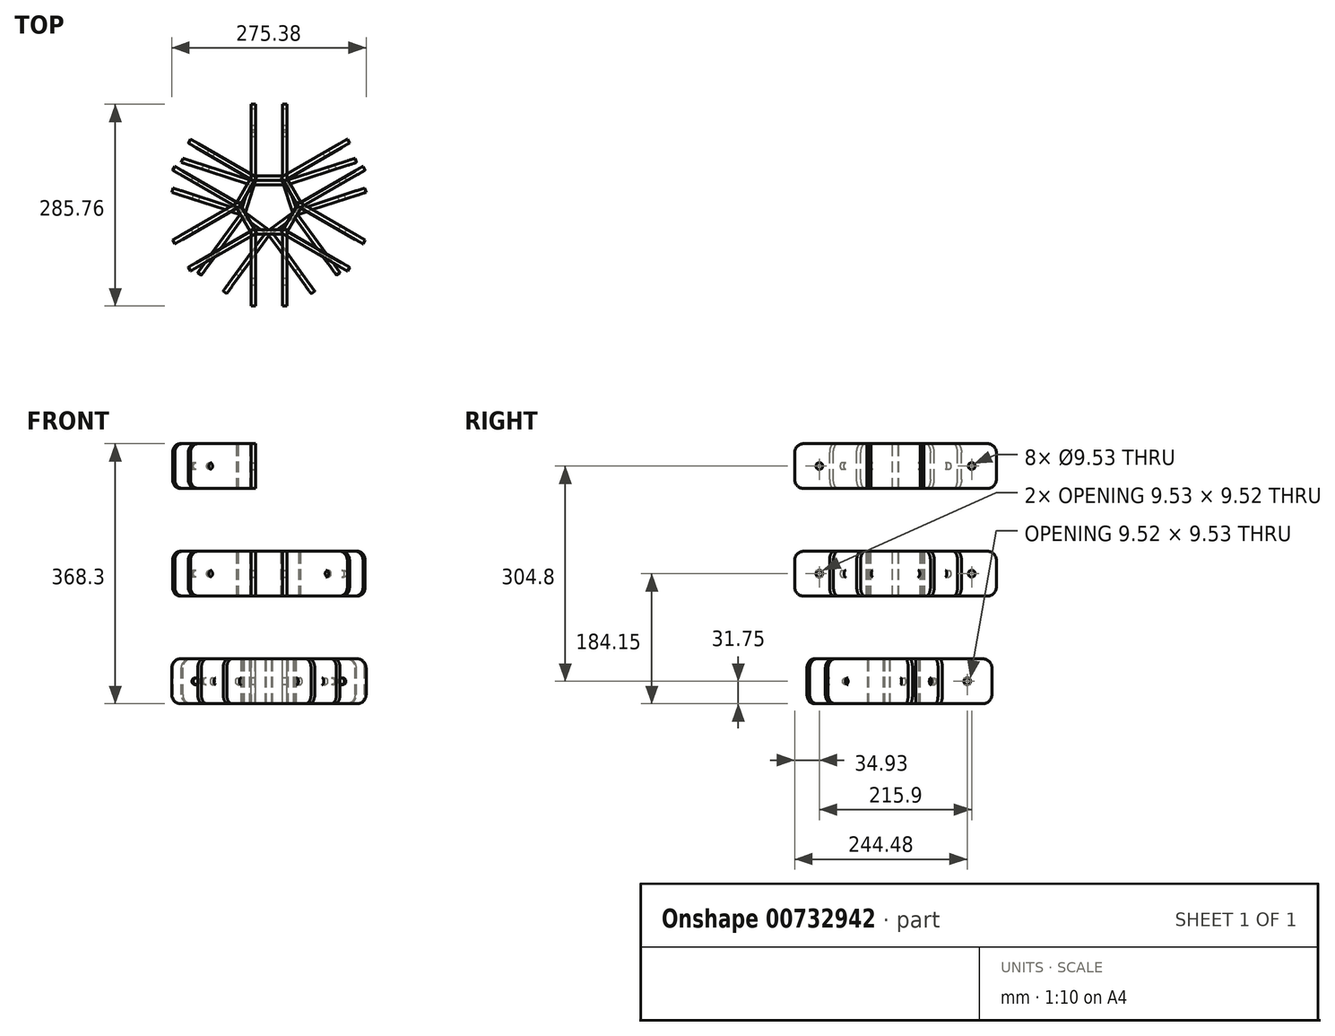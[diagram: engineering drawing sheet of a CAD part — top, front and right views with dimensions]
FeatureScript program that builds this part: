
annotation { "Feature Type Name" : "Feature", "Feature Type Description" : "" }
export const myFeature = defineFeature(function(context is Context, id is Id, definition is map)
    precondition{}
    {
        {
            var Q0;
            Q0=qCreatedBy(makeId("Top.planeOp"),FACE);
            var sketch = newSketch(context, id + "F0", { "sketchPlane" : qUnion([Q0])});
            skLineSegment(sketch, "E0.bottom", {"start": v(-25.4, 136.53) * mm, "end": v(-19.05, 136.53) * mm});
            skLineSegment(sketch, "E0.top", {"start": v(-25.4, 28.58) * mm, "end": v(25.4, 28.58) * mm});
            skLineSegment(sketch, "E0.left", {"start": v(-25.4, 136.53) * mm, "end": v(-25.4, 28.58) * mm});
            skLineSegment(sketch, "E0.right", {"start": v(25.4, 136.53) * mm, "end": v(25.4, 28.58) * mm});
            skLineSegment(sketch, "E1.bottom", {"start": v(19.05, 34.93) * mm, "end": v(-19.05, 34.93) * mm});
            skLineSegment(sketch, "E1.left", {"start": v(19.05, 34.93) * mm, "end": v(19.05, 136.53) * mm});
            skLineSegment(sketch, "E1.right", {"start": v(-19.05, 34.93) * mm, "end": v(-19.05, 136.53) * mm});
            skLineSegment(sketch, "E2.trimOffspring", {"start": v(19.05, 136.53) * mm, "end": v(25.4, 136.53) * mm});
            skSolve(sketch);
        }
        {
            var Q0;
            Q0 = qSketchRegion(id + "F0", true);
            extrude(context, id + "F1", {"entities" : qUnion([Q0]), "oppositeDirection" : true, "depth" : 63.5 * mm, "offsetDistance" : 25.4 * mm});
        }
        {
            var Q0;
            Q0=makeQuery(id+"F1.opExtrude","SWEPT_FACE",FACE,{"disambiguationData":[OSD([sQuery(id+"F0.wireOp",EDGE,"E0.left")])]});
            var sketch = newSketch(context, id + "F2", { "sketchPlane" : qUnion([Q0])});
            skCircle(sketch, "E3", {"center": v(-101.6, -31.75) * mm, "radius": 4.76 * mm});
            skSolve(sketch);
        }
        {
            var Q0;
            Q0 = qSketchRegion(id + "F2", true);
            extrude(context, id + "F3", {"entities" : qUnion([Q0]), "operationType" : NewBodyOperationType.REMOVE, "endBound" : BoundingType.THROUGH_ALL, "oppositeDirection" : true, "depth" : 25.4 * mm, "offsetDistance" : 25.4 * mm});
        }
        {
            var Q0;
            Q0=qCreatedBy(makeId("Right.planeOp"),FACE);
            var sketch = newSketch(context, id + "F4", { "sketchPlane" : qUnion([Q0])});
            skLineSegment(sketch, "E4", {"start": v(0, 0) * mm, "end": v(0, 467.4) * mm, "construction": true});
            skSolve(sketch);
        }
        {
            var Q0;
            Q0=makeQuery(id+"F1.opExtrude","CAP_EDGE",EDGE,{"disambiguationData":[OSD([sQuery(id+"F0.wireOp",EDGE,"E0.bottom")])],"isStart":false});
            var Q1;
            Q1=makeQuery(id+"F1.opExtrude","CAP_EDGE",EDGE,{"disambiguationData":[OSD([sQuery(id+"F0.wireOp",EDGE,"E2.trimOffspring")])],"isStart":false});
            var Q2;
            Q2=makeQuery(id+"F1.opExtrude","CAP_EDGE",EDGE,{"disambiguationData":[OSD([sQuery(id+"F0.wireOp",EDGE,"E2.trimOffspring")])],"isStart":true});
            var Q3;
            Q3=makeQuery(id+"F1.opExtrude","CAP_EDGE",EDGE,{"disambiguationData":[OSD([sQuery(id+"F0.wireOp",EDGE,"E0.bottom")])],"isStart":true});
            fillet(context, id + "F5", {"entities" : qUnion([Q0, Q1, Q2, Q3]), "radius" : 12.7 * mm, "tangentPropagation" : true, "allowEdgeOverflow" : false});
        }
        {
            var Q0;
            Q0=makeQuery(id+"F1.opExtrude","SWEPT_BODY",BODY,{"disambiguationData":[OSD([sQuery(id+"F0.wireOp",EDGE,"E0.bottom"),sQuery(id+"F0.wireOp",EDGE,"E0.top"),sQuery(id+"F0.wireOp",EDGE,"E0.left"),sQuery(id+"F0.wireOp",EDGE,"E0.right"),sQuery(id+"F0.wireOp",EDGE,"E1.bottom"),sQuery(id+"F0.wireOp",EDGE,"E1.left"),sQuery(id+"F0.wireOp",EDGE,"E1.right"),sQuery(id+"F0.wireOp",EDGE,"E2.trimOffspring")])]});
            transform(context, id + "F6", {"entities" : qUnion([Q0]), "transformType" : TransformType.TRANSLATION_3D, "dx" : 0 * mm, "dy" : 6.35 * mm, "dz" : 152.4 * mm, "makeCopy" : true});
        }
        {
            var Q0;
            Q0=makeQuery(id+"F6.opPattern","COPY",BODY,{"derivedFrom":makeQuery(id+"F1.opExtrude","SWEPT_BODY",BODY,{"disambiguationData":[OSD([sQuery(id+"F0.wireOp",EDGE,"E0.bottom"),sQuery(id+"F0.wireOp",EDGE,"E0.top"),sQuery(id+"F0.wireOp",EDGE,"E0.left"),sQuery(id+"F0.wireOp",EDGE,"E0.right"),sQuery(id+"F0.wireOp",EDGE,"E1.bottom"),sQuery(id+"F0.wireOp",EDGE,"E1.left"),sQuery(id+"F0.wireOp",EDGE,"E1.right"),sQuery(id+"F0.wireOp",EDGE,"E2.trimOffspring")])]}),"instanceName":"1"});
            transform(context, id + "F7", {"entities" : qUnion([Q0]), "transformType" : TransformType.TRANSLATION_3D, "dx" : 0 * mm, "dy" : 0 * mm, "dz" : 152.4 * mm, "makeCopy" : true});
        }
        {
            var Q0;
            Q0=makeQuery(id+"F1.opExtrude","SWEPT_BODY",BODY,{"disambiguationData":[OSD([sQuery(id+"F0.wireOp",EDGE,"E0.bottom"),sQuery(id+"F0.wireOp",EDGE,"E0.top"),sQuery(id+"F0.wireOp",EDGE,"E0.left"),sQuery(id+"F0.wireOp",EDGE,"E0.right"),sQuery(id+"F0.wireOp",EDGE,"E1.bottom"),sQuery(id+"F0.wireOp",EDGE,"E1.left"),sQuery(id+"F0.wireOp",EDGE,"E1.right"),sQuery(id+"F0.wireOp",EDGE,"E2.trimOffspring")])]});
            var Q1;
            Q1=sQuery(id+"F4.wireOp",EDGE,"E4");
            circularPattern(context, id + "F8", {"operationType" : NewBodyOperationType.ADD, "entities" : qUnion([Q0]), "axis" : qUnion([Q1]), "angle" : 360 * degree, "instanceCount" : 5, "equalSpace" : true});
        }
        {
            var Q0;
            Q0=makeQuery(id+"F6.opPattern","COPY",BODY,{"derivedFrom":makeQuery(id+"F1.opExtrude","SWEPT_BODY",BODY,{"disambiguationData":[OSD([sQuery(id+"F0.wireOp",EDGE,"E0.bottom"),sQuery(id+"F0.wireOp",EDGE,"E0.top"),sQuery(id+"F0.wireOp",EDGE,"E0.left"),sQuery(id+"F0.wireOp",EDGE,"E0.right"),sQuery(id+"F0.wireOp",EDGE,"E1.bottom"),sQuery(id+"F0.wireOp",EDGE,"E1.left"),sQuery(id+"F0.wireOp",EDGE,"E1.right"),sQuery(id+"F0.wireOp",EDGE,"E2.trimOffspring")])]}),"instanceName":"1"});
            var Q1;
            Q1=sQuery(id+"F4.wireOp",EDGE,"E4");
            circularPattern(context, id + "F9", {"operationType" : NewBodyOperationType.ADD, "entities" : qUnion([Q0]), "axis" : qUnion([Q1]), "angle" : 360 * degree, "instanceCount" : 6, "equalSpace" : true});
        }
        {
            var Q0;
            Q0=makeQuery(id+"F7.opPattern","COPY",BODY,{"derivedFrom":makeQuery(id+"F6.opPattern","COPY",BODY,{"derivedFrom":makeQuery(id+"F1.opExtrude","SWEPT_BODY",BODY,{"disambiguationData":[OSD([sQuery(id+"F0.wireOp",EDGE,"E0.bottom"),sQuery(id+"F0.wireOp",EDGE,"E0.top"),sQuery(id+"F0.wireOp",EDGE,"E0.left"),sQuery(id+"F0.wireOp",EDGE,"E0.right"),sQuery(id+"F0.wireOp",EDGE,"E1.bottom"),sQuery(id+"F0.wireOp",EDGE,"E1.left"),sQuery(id+"F0.wireOp",EDGE,"E1.right"),sQuery(id+"F0.wireOp",EDGE,"E2.trimOffspring")])]}),"instanceName":"1"}),"instanceName":"1"});
            var Q1;
            Q1=sQuery(id+"F4.wireOp",EDGE,"E4");
            circularPattern(context, id + "F10", {"operationType" : NewBodyOperationType.ADD, "entities" : qUnion([Q0]), "axis" : qUnion([Q1]), "angle" : 180 * degree, "instanceCount" : 4, "equalSpace" : true});
        }
        {
            var Q0;
            Q0=makeQuery(id+"F10.opPattern","COPY",FACE,{"derivedFrom":makeQuery(id+"F7.opPattern","COPY",FACE,{"derivedFrom":makeQuery(id+"F6.opPattern","COPY",FACE,{"derivedFrom":makeQuery(id+"F1.opExtrude","SWEPT_FACE",FACE,{"disambiguationData":[OSD([sQuery(id+"F0.wireOp",EDGE,"E0.left")])]}),"instanceName":"1"}),"instanceName":"1"}),"instanceName":"3"});
            var sketch = newSketch(context, id + "F11", { "sketchPlane" : qUnion([Q0])});
            skLineSegment(sketch, "E5.bottom", {"start": v(-142.88, 304.8) * mm, "end": v(142.88, 304.8) * mm});
            skLineSegment(sketch, "E5.top", {"start": v(-142.88, 241.3) * mm, "end": v(142.88, 241.3) * mm});
            skLineSegment(sketch, "E5.left", {"start": v(-142.88, 304.8) * mm, "end": v(-142.88, 241.3) * mm});
            skLineSegment(sketch, "E5.right", {"start": v(142.88, 304.8) * mm, "end": v(142.88, 241.3) * mm});
            skSolve(sketch);
        }
        {
            var Q0;
            Q0 = qSketchRegion(id + "F11", true);
            var Q1;
            Q1=makeQuery(id+"F10.opPattern","COPY",FACE,{"derivedFrom":makeQuery(id+"F7.opPattern","COPY",FACE,{"derivedFrom":makeQuery(id+"F6.opPattern","COPY",FACE,{"derivedFrom":makeQuery(id+"F1.opExtrude","SWEPT_FACE",FACE,{"disambiguationData":[OSD([sQuery(id+"F0.wireOp",EDGE,"E1.left")])]}),"instanceName":"1"}),"instanceName":"1"}),"instanceName":"3"});
            extrude(context, id + "F12", {"entities" : qUnion([Q0]), "operationType" : NewBodyOperationType.REMOVE, "endBound" : BoundingType.UP_TO_SURFACE, "oppositeDirection" : true, "depth" : 25.4 * mm, "endBoundEntityFace" : qUnion([Q1]), "offsetDistance" : 25.4 * mm});
        }
    });
